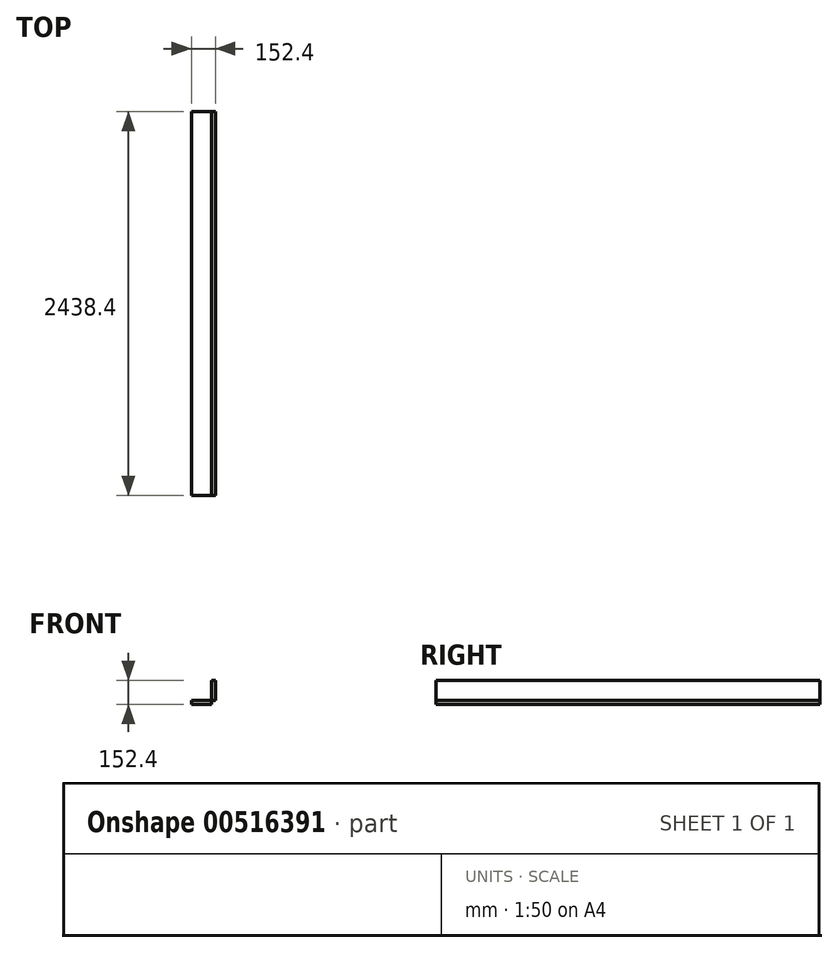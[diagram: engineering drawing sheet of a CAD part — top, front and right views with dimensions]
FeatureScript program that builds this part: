
annotation { "Feature Type Name" : "Feature", "Feature Type Description" : "" }
export const myFeature = defineFeature(function(context is Context, id is Id, definition is map)
    precondition{}
    {
        {
            var Q0;
            Q0=qCreatedBy(makeId("Front.planeOp"),FACE);
            var sketch = newSketch(context, id + "F0", { "sketchPlane" : qUnion([Q0])});
            skLineSegment(sketch, "E0.bottom", {"start": v(0, 0) * mm, "end": v(-25.4, 0) * mm});
            skLineSegment(sketch, "E0.top", {"start": v(0, 152.4) * mm, "end": v(-25.4, 152.4) * mm});
            skLineSegment(sketch, "E0.left", {"start": v(0, 0) * mm, "end": v(0, 152.4) * mm});
            skLineSegment(sketch, "E0.right", {"start": v(-25.4, 0) * mm, "end": v(-25.4, 152.4) * mm});
            skLineSegment(sketch, "E1.bottom", {"start": v(0, 0) * mm, "end": v(-152.4, 0) * mm});
            skLineSegment(sketch, "E1.top", {"start": v(0, 25.4) * mm, "end": v(-152.4, 25.4) * mm});
            skLineSegment(sketch, "E1.left", {"start": v(0, 0) * mm, "end": v(0, 25.4) * mm});
            skLineSegment(sketch, "E1.right", {"start": v(-152.4, 0) * mm, "end": v(-152.4, 25.4) * mm});
            skSolve(sketch);
        }
        {
            var Q0;
            {var subQ0=sQuery(id+"F0.wireOp",EDGE,"E0.top");Q0=makeQuery(id+"F0.imprint","IMPRINT",FACE,{"disambiguationData":[TD([[makeQuery(id+"F0.imprint","IMPRINT",EDGE,{"derivedFrom":subQ0}),1.0]])]});}
            var Q1;
            {var subQ5=sQuery(id+"F0.wireOp",EDGE,"E1.right");Q1=makeQuery(id+"F0.imprint","IMPRINT",FACE,{"disambiguationData":[TD([[makeQuery(id+"F0.imprint","IMPRINT",EDGE,{"derivedFrom":subQ5}),-1.0]])]});}
            var Q2;
            {var subQ5=sQuery(id+"F0.wireOp",EDGE,"E1.left");Q2=makeQuery(id+"F0.imprint","IMPRINT",FACE,{"disambiguationData":[TD([[makeQuery(id+"F0.imprint","IMPRINT",EDGE,{"derivedFrom":subQ5}),1.0]])]});}
            extrude(context, id + "F1", {"entities" : qUnion([Q0, Q1, Q2]), "depth" : 2438.4 * mm, "offsetDistance" : 25.4 * mm});
        }
    });
